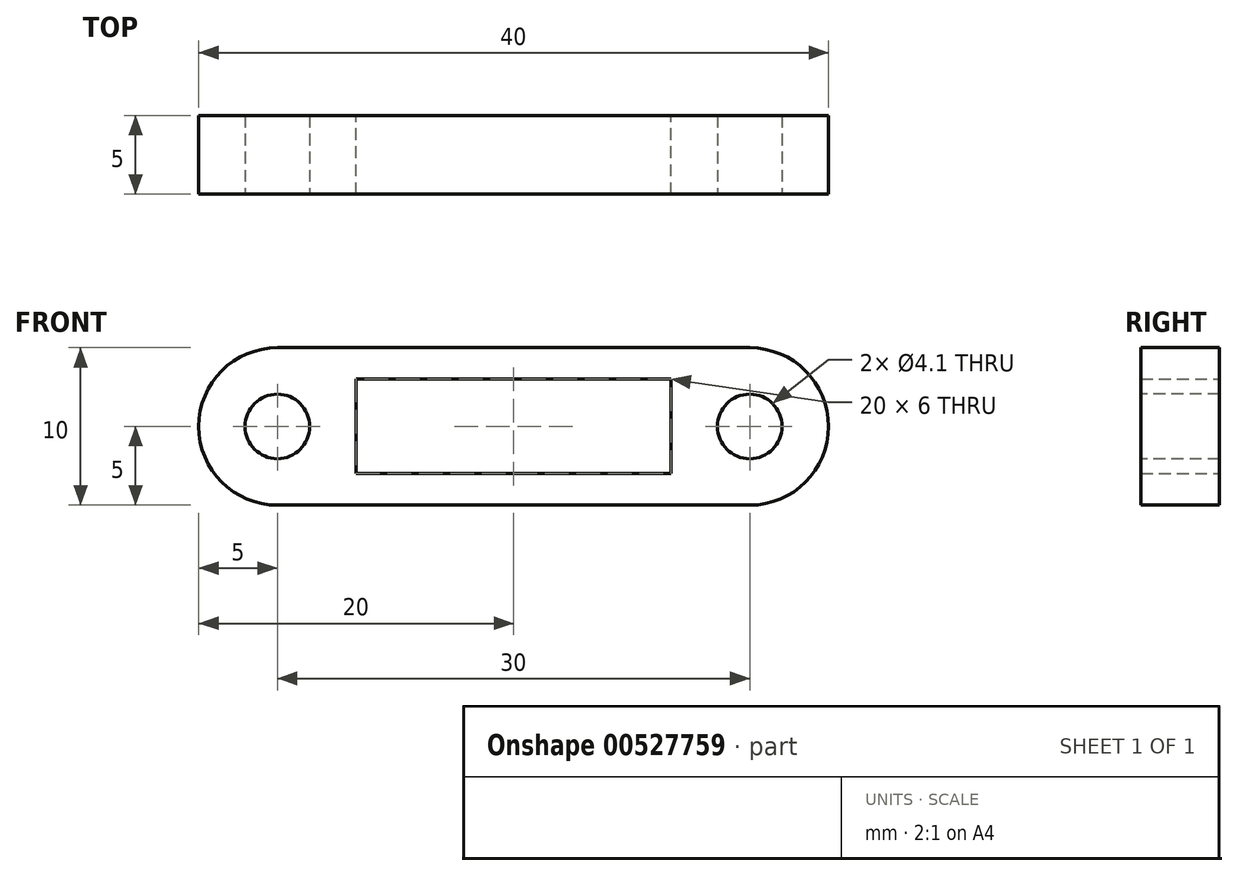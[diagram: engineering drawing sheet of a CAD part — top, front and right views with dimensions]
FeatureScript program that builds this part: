
annotation { "Feature Type Name" : "Feature", "Feature Type Description" : "" }
export const myFeature = defineFeature(function(context is Context, id is Id, definition is map)
    precondition{}
    {
        {
            var Q0;
            Q0=qCreatedBy(makeId("Top.planeOp"),FACE);
            var sketch = newSketch(context, id + "F0", { "sketchPlane" : qUnion([Q0])});
            skLineSegment(sketch, "E0.bottom", {"start": v(0, 0) * mm, "end": v(40, 0) * mm});
            skLineSegment(sketch, "E0.top", {"start": v(0, 5) * mm, "end": v(40, 5) * mm});
            skLineSegment(sketch, "E0.left", {"start": v(0, 0) * mm, "end": v(0, 5) * mm});
            skLineSegment(sketch, "E0.right", {"start": v(40, 0) * mm, "end": v(40, 5) * mm});
            skSolve(sketch);
        }
        {
            var Q0;
            Q0 = qSketchRegion(id + "F0", true);
            extrude(context, id + "F1", {"entities" : qUnion([Q0]), "depth" : 10 * mm, "offsetDistance" : 25 * mm});
        }
        {
            var Q0;
            Q0=makeQuery(id+"F1.opExtrude","SWEPT_FACE",FACE,{"disambiguationData":[OSD([sQuery(id+"F0.wireOp",EDGE,"E0.bottom")])]});
            var sketch = newSketch(context, id + "F2", { "sketchPlane" : qUnion([Q0])});
            skCircle(sketch, "E1", {"center": v(5, 5) * mm, "radius": 2.05 * mm});
            skSolve(sketch);
        }
        {
            var Q0;
            Q0 = qSketchRegion(id + "F2", true);
            extrude(context, id + "F3", {"entities" : qUnion([Q0]), "operationType" : NewBodyOperationType.REMOVE, "oppositeDirection" : true, "depth" : 25 * mm, "offsetDistance" : 25 * mm});
        }
        {
            var Q0;
            Q0=makeQuery(id+"F1.opExtrude","SWEPT_FACE",FACE,{"disambiguationData":[OSD([sQuery(id+"F0.wireOp",EDGE,"E0.bottom")])]});
            var sketch = newSketch(context, id + "F4", { "sketchPlane" : qUnion([Q0])});
            skCircle(sketch, "E2", {"center": v(35, 5) * mm, "radius": 2.05 * mm});
            skSolve(sketch);
        }
        {
            var Q0;
            Q0 = qSketchRegion(id + "F4", true);
            extrude(context, id + "F5", {"entities" : qUnion([Q0]), "operationType" : NewBodyOperationType.REMOVE, "oppositeDirection" : true, "depth" : 25 * mm, "offsetDistance" : 25 * mm});
        }
        {
            var Q0;
            Q0=makeQuery(id+"F1.opExtrude","CAP_EDGE",EDGE,{"disambiguationData":[OSD([sQuery(id+"F0.wireOp",EDGE,"E0.left")])],"isStart":false});
            var Q1;
            Q1=makeQuery(id+"F1.opExtrude","CAP_EDGE",EDGE,{"disambiguationData":[OSD([sQuery(id+"F0.wireOp",EDGE,"E0.left")])],"isStart":true});
            var Q2;
            Q2=makeQuery(id+"F1.opExtrude","CAP_EDGE",EDGE,{"disambiguationData":[OSD([sQuery(id+"F0.wireOp",EDGE,"E0.right")])],"isStart":false});
            var Q3;
            Q3=makeQuery(id+"F1.opExtrude","CAP_EDGE",EDGE,{"disambiguationData":[OSD([sQuery(id+"F0.wireOp",EDGE,"E0.right")])],"isStart":true});
            fillet(context, id + "F6", {"entities" : qUnion([Q0, Q1, Q2, Q3]), "radius" : 5 * mm, "tangentPropagation" : true, "allowEdgeOverflow" : false});
        }
        {
            var Q0;
            Q0=makeQuery(id+"F1.opExtrude","SWEPT_FACE",FACE,{"disambiguationData":[OSD([sQuery(id+"F0.wireOp",EDGE,"E0.top")])]});
            var sketch = newSketch(context, id + "F7", { "sketchPlane" : qUnion([Q0])});
            skLineSegment(sketch, "E3.bottom", {"start": v(-30, 2) * mm, "end": v(-10, 2) * mm});
            skLineSegment(sketch, "E3.top", {"start": v(-30, 8) * mm, "end": v(-10, 8) * mm});
            skLineSegment(sketch, "E3.left", {"start": v(-30, 2) * mm, "end": v(-30, 8) * mm});
            skLineSegment(sketch, "E3.right", {"start": v(-10, 2) * mm, "end": v(-10, 8) * mm});
            skSolve(sketch);
        }
        {
            var Q0;
            Q0 = qSketchRegion(id + "F7", true);
            extrude(context, id + "F8", {"entities" : qUnion([Q0]), "operationType" : NewBodyOperationType.REMOVE, "oppositeDirection" : true, "depth" : 25 * mm, "offsetDistance" : 25 * mm});
        }
    });
